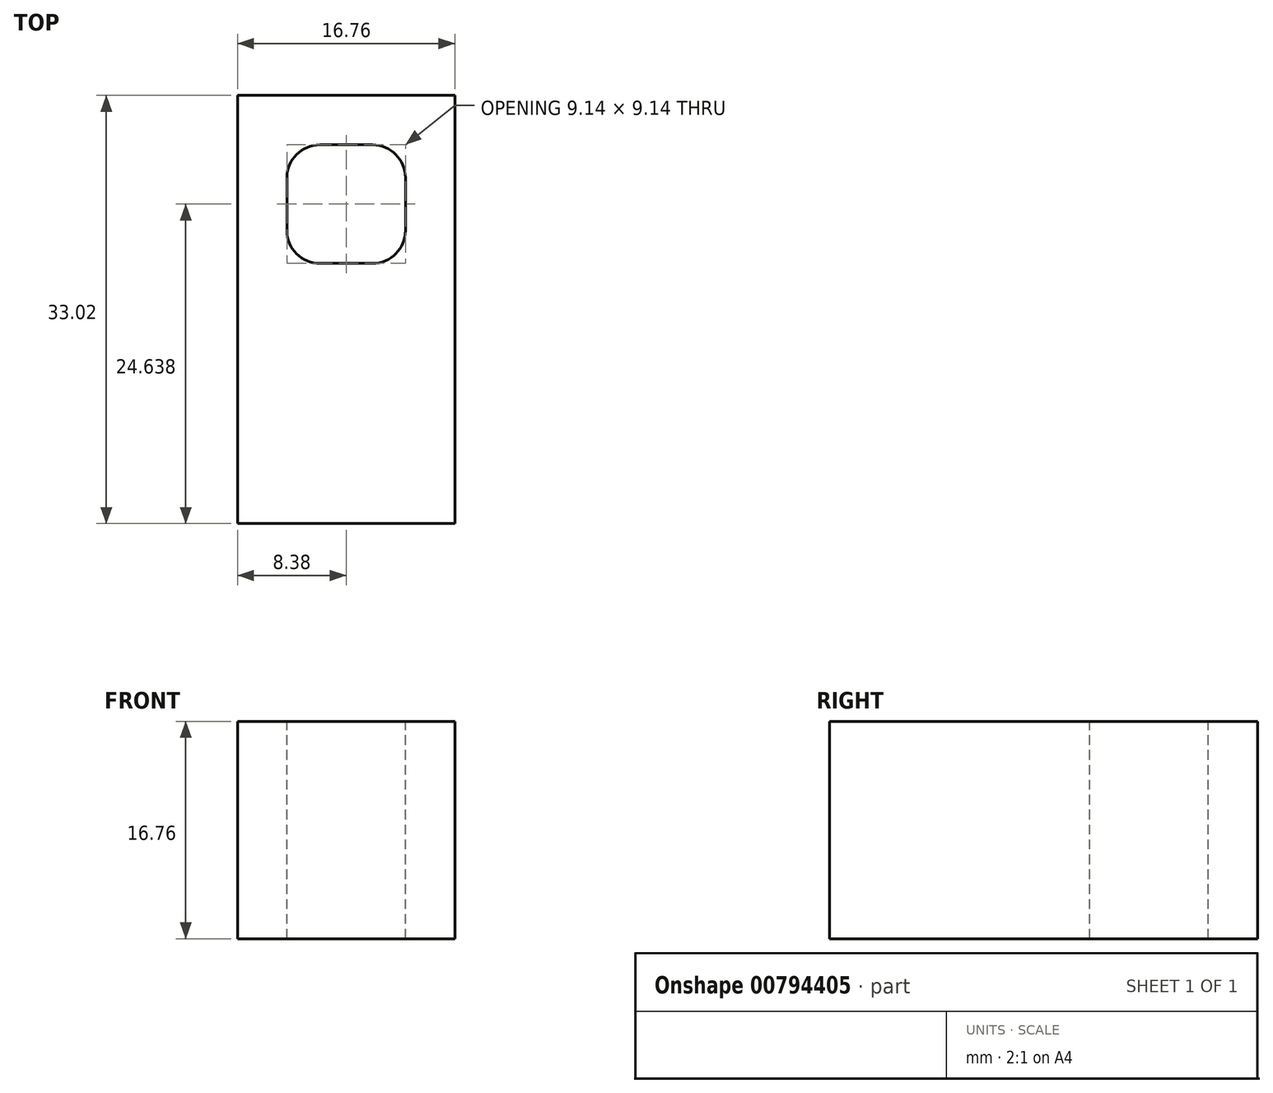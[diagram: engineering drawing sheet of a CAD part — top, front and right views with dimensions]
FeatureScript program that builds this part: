
annotation { "Feature Type Name" : "Feature", "Feature Type Description" : "" }
export const myFeature = defineFeature(function(context is Context, id is Id, definition is map)
    precondition{}
    {
        {
            var Q0;
            Q0=qCreatedBy(makeId("Top.planeOp"),FACE);
            var sketch = newSketch(context, id + "F0", { "sketchPlane" : qUnion([Q0])});
            skLineSegment(sketch, "E0.bottom", {"start": v(-8.38, 16.51) * mm, "end": v(8.38, 16.51) * mm});
            skLineSegment(sketch, "E0.top", {"start": v(-8.38, -16.51) * mm, "end": v(8.38, -16.51) * mm});
            skLineSegment(sketch, "E0.left", {"start": v(-8.38, 16.51) * mm, "end": v(-8.38, -16.51) * mm});
            skLineSegment(sketch, "E0.right", {"start": v(8.38, 16.5) * mm, "end": v(8.38, -16.51) * mm});
            skPoint(sketch, "E0.middle", {"position": v(0, 0) * mm});
            skSolve(sketch);
        }
        {
            var Q0;
            Q0=makeQuery(id+"F0.imprint","IMPRINT",FACE,{"disambiguationData":[TD([[makeQuery(id+"F0.imprint","IMPRINT",EDGE,{"derivedFrom":sQuery(id+"F0.wireOp",EDGE,"E0.bottom")}),-1.0]])]});
            extrude(context, id + "F1", {"entities" : qUnion([Q0]), "endBound" : BoundingType.SYMMETRIC, "depth" : 16.76 * mm, "offsetDistance" : 25.4 * mm});
        }
        {
            var Q0;
            Q0=makeQuery(id+"F1.opExtrude","CAP_FACE",FACE,{"disambiguationData":[OSD([sQuery(id+"F0.wireOp",EDGE,"E0.bottom"),sQuery(id+"F0.wireOp",EDGE,"E0.top"),sQuery(id+"F0.wireOp",EDGE,"E0.left"),sQuery(id+"F0.wireOp",EDGE,"E0.right")])],"isStart":false});
            var sketch = newSketch(context, id + "F2", { "sketchPlane" : qUnion([Q0])});
            skLineSegment(sketch, "E1.bottom", {"start": v(-4.57, 3.56) * mm, "end": v(4.57, 3.56) * mm});
            skLineSegment(sketch, "E1.top", {"start": v(-4.57, 12.7) * mm, "end": v(4.57, 12.7) * mm});
            skLineSegment(sketch, "E1.left", {"start": v(-4.57, 3.56) * mm, "end": v(-4.57, 12.7) * mm});
            skLineSegment(sketch, "E1.right", {"start": v(4.57, 3.56) * mm, "end": v(4.57, 12.7) * mm});
            skPoint(sketch, "E1.middle", {"position": v(0, 8.13) * mm});
            skSolve(sketch);
        }
        {
            var Q0;
            Q0=makeQuery(id+"F2.imprint","IMPRINT",FACE,{"disambiguationData":[TD([[makeQuery(id+"F2.imprint","IMPRINT",EDGE,{"derivedFrom":sQuery(id+"F2.wireOp",EDGE,"E1.bottom")}),1.0]])]});
            extrude(context, id + "F3", {"entities" : qUnion([Q0]), "operationType" : NewBodyOperationType.REMOVE, "oppositeDirection" : true, "depth" : 25.4 * mm, "offsetDistance" : 25.4 * mm});
        }
        {
            var Q0;
            Q0=makeQuery(id+"F3.boolean.opBoolean","COPY",EDGE,{"derivedFrom":makeQuery(id+"F3.opExtrude","SWEPT_EDGE",EDGE,{"disambiguationData":[OSD([sQuery(id+"F2.wireOp",EDGE,"E1.top"),sQuery(id+"F2.wireOp",EDGE,"E1.left")])]})});
            var Q1;
            Q1=makeQuery(id+"F3.boolean.opBoolean","COPY",EDGE,{"derivedFrom":makeQuery(id+"F3.opExtrude","SWEPT_EDGE",EDGE,{"disambiguationData":[OSD([sQuery(id+"F2.wireOp",EDGE,"E1.top"),sQuery(id+"F2.wireOp",EDGE,"E1.right")])]})});
            var Q2;
            Q2=makeQuery(id+"Fa3J6VauDzyZfbK_1.1.F3.boolean.opBoolean","COPY",EDGE,{"derivedFrom":makeQuery(id+"Fa3J6VauDzyZfbK_1.1.F3.opExtrude","SWEPT_EDGE",EDGE,{"disambiguationData":[OSD([sQuery(id+"F2.wireOp",EDGE,"E1.bottom"),sQuery(id+"F2.wireOp",EDGE,"E1.right")])]})});
            var Q3;
            Q3=makeQuery(id+"Fa3J6VauDzyZfbK_1.1.F3.boolean.opBoolean","COPY",EDGE,{"derivedFrom":makeQuery(id+"Fa3J6VauDzyZfbK_1.1.F3.opExtrude","SWEPT_EDGE",EDGE,{"disambiguationData":[OSD([sQuery(id+"F2.wireOp",EDGE,"E1.bottom"),sQuery(id+"F2.wireOp",EDGE,"E1.left")])]})});
            var Q4;
            Q4=makeQuery(id+"F3.boolean.opBoolean","COPY",EDGE,{"derivedFrom":makeQuery(id+"F3.opExtrude","SWEPT_EDGE",EDGE,{"disambiguationData":[OSD([sQuery(id+"F2.wireOp",EDGE,"E1.bottom"),sQuery(id+"F2.wireOp",EDGE,"E1.left")])]})});
            var Q5;
            Q5=makeQuery(id+"Fa3J6VauDzyZfbK_1.1.F3.boolean.opBoolean","COPY",EDGE,{"derivedFrom":makeQuery(id+"Fa3J6VauDzyZfbK_1.1.F3.opExtrude","SWEPT_EDGE",EDGE,{"disambiguationData":[OSD([sQuery(id+"F2.wireOp",EDGE,"E1.top"),sQuery(id+"F2.wireOp",EDGE,"E1.left")])]})});
            fillet(context, id + "F4", {"entities" : qUnion([Q0, Q1, Q2, Q3, Q4, Q5]), "radius" : 2.54 * mm, "tangentPropagation" : true, "allowEdgeOverflow" : false});
        }
        {
            var Q0;
            Q0=makeQuery(id+"Fa3J6VauDzyZfbK_1.1.F3.boolean.opBoolean","COPY",EDGE,{"derivedFrom":makeQuery(id+"Fa3J6VauDzyZfbK_1.1.F3.opExtrude","SWEPT_EDGE",EDGE,{"disambiguationData":[OSD([sQuery(id+"F2.wireOp",EDGE,"E1.top"),sQuery(id+"F2.wireOp",EDGE,"E1.right")])]})});
            var Q1;
            Q1=makeQuery(id+"F3.boolean.opBoolean","COPY",EDGE,{"derivedFrom":makeQuery(id+"F3.opExtrude","SWEPT_EDGE",EDGE,{"disambiguationData":[OSD([sQuery(id+"F2.wireOp",EDGE,"E1.bottom"),sQuery(id+"F2.wireOp",EDGE,"E1.right")])]})});
            fillet(context, id + "F5", {"entities" : qUnion([Q0, Q1]), "radius" : 2.54 * mm, "tangentPropagation" : true, "allowEdgeOverflow" : false});
        }
    });
